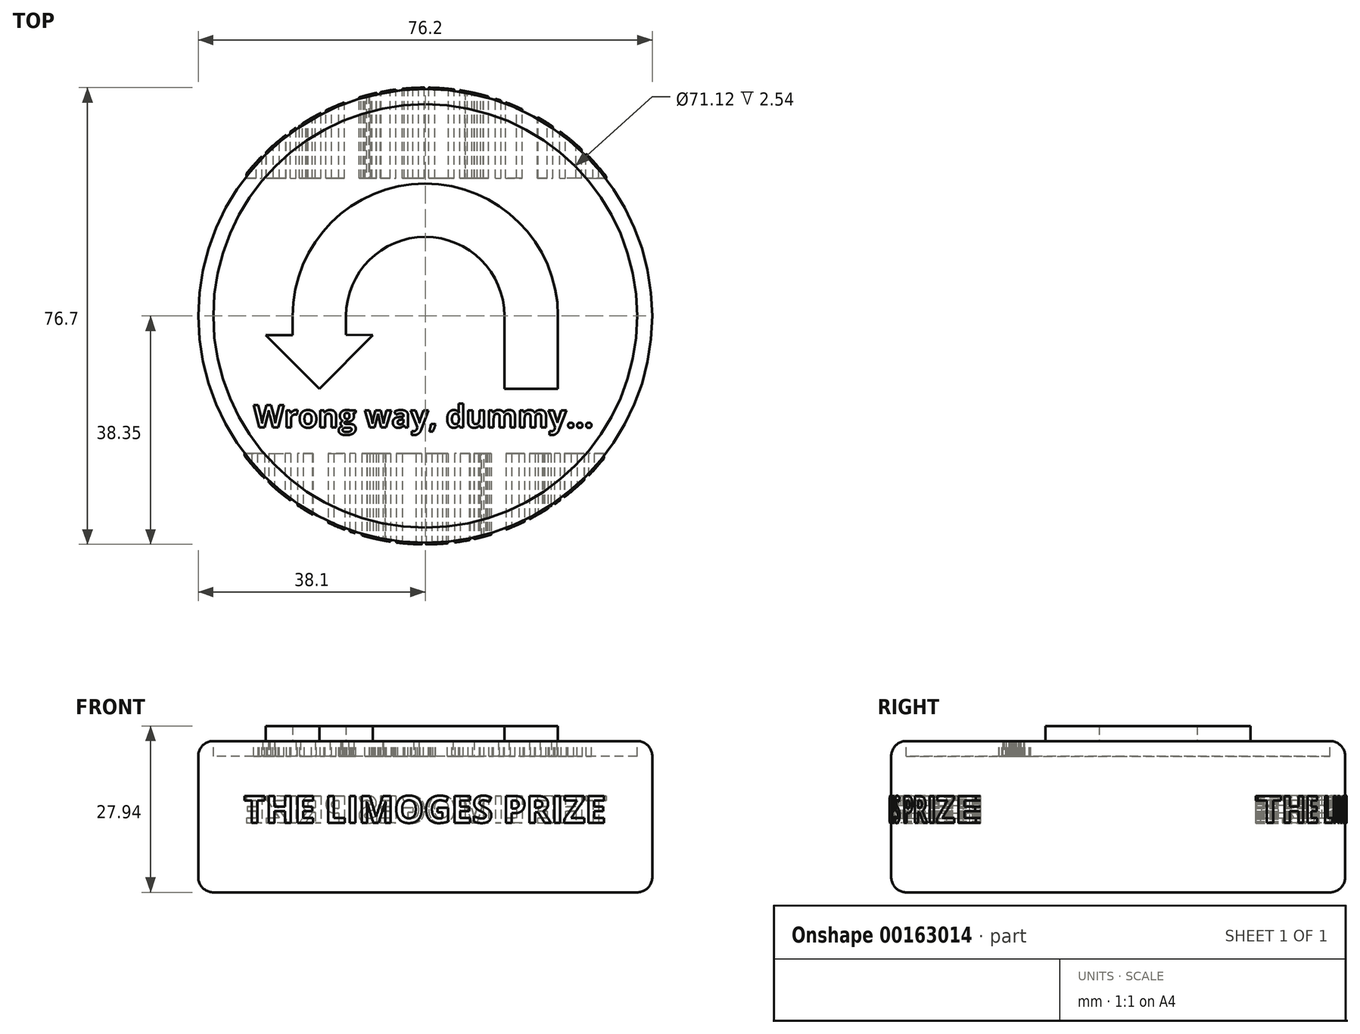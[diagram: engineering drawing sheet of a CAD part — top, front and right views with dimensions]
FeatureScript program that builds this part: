
annotation { "Feature Type Name" : "Feature", "Feature Type Description" : "" }
export const myFeature = defineFeature(function(context is Context, id is Id, definition is map)
    precondition{}
    {
        {
            var Q0;
            Q0=qCreatedBy(makeId("Top.planeOp"),FACE);
            var sketch = newSketch(context, id + "F0", { "sketchPlane" : qUnion([Q0])});
            skCircle(sketch, "E0", {"center": v(0, 0) * mm, "radius": 38.1 * mm});
            skSolve(sketch);
        }
        {
            var Q0;
            Q0 = qSketchRegion(id + "F0", true);
            var Q1;
            Q1=makeQuery(id+"F0.imprint","IMPRINT",FACE,{"disambiguationData":[TD([[makeQuery(id+"F0.imprint","IMPRINT",EDGE,{"derivedFrom":sQuery(id+"F0.wireOp",EDGE,"E0")}),1.0]])]});
            extrude(context, id + "F1", {"entities" : qUnion([Q0, Q1]), "depth" : 25.4 * mm});
        }
        {
            var Q0;
            Q0=makeQuery(id+"F1.opExtrude","CAP_EDGE",EDGE,{"disambiguationData":[OSD([sQuery(id+"F0.wireOp",EDGE,"E0")])],"isStart":false});
            var Q1;
            Q1=makeQuery(id+"F1.opExtrude","CAP_EDGE",EDGE,{"disambiguationData":[OSD([sQuery(id+"F0.wireOp",EDGE,"E0")])],"isStart":true});
            fillet(context, id + "F2", {"entities" : qUnion([Q0, Q1]), "radius" : 2.54 * mm, "tangentPropagation" : true, "allowEdgeOverflow" : false});
        }
        {
            var Q0;
            Q0=makeQuery(id+"F1.opExtrude","CAP_FACE",FACE,{"disambiguationData":[OSD([sQuery(id+"F0.wireOp",EDGE,"E0")])],"isStart":false});
            var sketch = newSketch(context, id + "F3", { "sketchPlane" : qUnion([Q0])});
            skLineSegment(sketch, "E1", {"start": v(-17.78, -12.2) * mm, "end": v(-22.28, -7.7) * mm});
            skLineSegment(sketch, "E2", {"start": v(-17.78, -12.2) * mm, "end": v(-13.28, -7.7) * mm});
            skLineSegment(sketch, "E3", {"start": v(-13.28, -7.7) * mm, "end": v(-8.8, -3.22) * mm});
            skLineSegment(sketch, "E4", {"start": v(-22.28, -7.7) * mm, "end": v(-26.76, -3.22) * mm});
            skLineSegment(sketch, "E5", {"start": v(-26.76, -3.22) * mm, "end": v(-22.28, -3.22) * mm});
            skLineSegment(sketch, "E6", {"start": v(-8.8, -3.22) * mm, "end": v(-13.28, -3.18) * mm});
            skLineSegment(sketch, "E7", {"start": v(17.78, -12.2) * mm, "end": v(22.28, -12.2) * mm});
            skLineSegment(sketch, "E8", {"start": v(17.78, -12.2) * mm, "end": v(13.28, -12.2) * mm});
            skLineSegment(sketch, "E9", {"start": v(13.28, -12.2) * mm, "end": v(13.28, 0) * mm});
            skLineSegment(sketch, "E10", {"start": v(22.28, -12.2) * mm, "end": v(22.28, 0) * mm});
            skLineSegment(sketch, "E11", {"start": v(-13.28, -3.18) * mm, "end": v(-13.28, 0) * mm});
            skLineSegment(sketch, "E12", {"start": v(-22.28, -3.22) * mm, "end": v(-22.28, -0.05) * mm});
            skArc(sketch, "E13", {"start": v(-22.28, -0.05) * mm, "mid": v(-0.02, 22.23) * mm, "end": v(22.28, 0) * mm});
            skArc(sketch, "E14", {"start": v(-13.28, 0) * mm, "mid": v(0, 13.28) * mm, "end": v(13.28, 0) * mm});
            skText(sketch, "E15", { "text": "Wrong way, dummy...", "fontName": "OpenSans-Bold.ttf"});
            const initialGuessF3  = {"E15": [-0.02883, -0.01873, 1, 0, 0.00381]};
            skSetInitialGuess(sketch, initialGuessF3);
            skSolve(sketch);
        }
        {
            var Q0;
            Q0=makeQuery(id+"F3.imprint","IMPRINT",FACE,{"disambiguationData":[TD([[makeQuery(id+"F3.imprint","IMPRINT",EDGE,{"derivedFrom":sQuery(id+"F3.wireOp",EDGE,"E1")}),-1.0]])]});
            var Q1;
            Q1=makeQuery(id+"F3.imprint","IMPRINT",FACE,{"disambiguationData":[TD([[makeQuery(id+"F3.imprint","IMPRINT",EDGE,{"derivedFrom":sQuery(id+"F3.wireOp",EDGE,"E1")}),1.0]])]});
            extrude(context, id + "F4", {"entities" : qUnion([Q0, Q1]), "operationType" : NewBodyOperationType.REMOVE, "oppositeDirection" : true, "depth" : 2.54 * mm});
        }
        {
            var Q0;
            Q0=makeQuery(id+"F3.imprint","IMPRINT",FACE,{"disambiguationData":[TD([[makeQuery(id+"F3.imprint","IMPRINT",EDGE,{"derivedFrom":sQuery(id+"F3.wireOp",EDGE,"E1")}),-1.0]])]});
            extrude(context, id + "F5", {"entities" : qUnion([Q0]), "operationType" : NewBodyOperationType.ADD, "depth" : 2.54 * mm});
        }
        {
            var Q0;
            Q0=makeQuery(id+"F3.imprint","IMPRINT",FACE,{"disambiguationData":[TD([[makeQuery(id+"F3.imprint","IMPRINT",EDGE,{"derivedFrom":sQuery(id+"F3.wireOp",EDGE,"E15.sketch_text.stroke-160")}),1.0]])]});
            var Q1;
            Q1=makeQuery(id+"F3.imprint","IMPRINT",FACE,{"disambiguationData":[TD([[makeQuery(id+"F3.imprint","IMPRINT",EDGE,{"derivedFrom":sQuery(id+"F3.wireOp",EDGE,"E15.sketch_text.stroke-110")}),1.0]])]});
            var Q2;
            Q2=makeQuery(id+"F3.imprint","IMPRINT",FACE,{"disambiguationData":[TD([[makeQuery(id+"F3.imprint","IMPRINT",EDGE,{"derivedFrom":sQuery(id+"F3.wireOp",EDGE,"E15.sketch_text.stroke-101")}),1.0]])]});
            var Q3;
            Q3=makeQuery(id+"F3.imprint","IMPRINT",FACE,{"disambiguationData":[TD([[makeQuery(id+"F3.imprint","IMPRINT",EDGE,{"derivedFrom":sQuery(id+"F3.wireOp",EDGE,"E15.sketch_text.stroke-37")}),1.0]])]});
            var Q4;
            Q4=makeQuery(id+"F3.imprint","IMPRINT",FACE,{"disambiguationData":[TD([[makeQuery(id+"F3.imprint","IMPRINT",EDGE,{"derivedFrom":sQuery(id+"F3.wireOp",EDGE,"E15.sketch_text.stroke-203")}),1.0]])]});
            extrude(context, id + "F6", {"entities" : qUnion([Q0, Q1, Q2, Q3, Q4]), "operationType" : NewBodyOperationType.REMOVE, "oppositeDirection" : true, "depth" : 2.54 * mm});
        }
        {
            var Q0;
            Q0=qCreatedBy(makeId("Front.planeOp"),FACE);
            cPlane(context, id + "F7", {"entities" : qUnion([Q0]), "cplaneType" : CPlaneType.OFFSET, "offset" : 38.35 * mm, "width" : 152.4 * mm, "height" : 152.4 * mm});
        }
        {
            var Q0;
            Q0=qCreatedBy(id+"F7.planeOp",FACE);
            var sketch = newSketch(context, id + "F8", { "sketchPlane" : qUnion([Q0])});
            skText(sketch, "E16", { "text": "THE LIMOGES PRIZE", "fontName": "OpenSans-Bold.ttf"});
            const initialGuessF8  = {"E16": [-0.03048, 0.01168, 1, 0, 0.00454]};
            skSetInitialGuess(sketch, initialGuessF8);
            skSolve(sketch);
        }
        {
            var Q0;
            Q0 = qSketchRegion(id + "F8", true);
            extrude(context, id + "F9", {"entities" : qUnion([Q0]), "oppositeDirection" : true, "depth" : 15.24 * mm});
        }
        {
            var Q0;
            Q0=qCreatedBy(makeId("Top.planeOp"),FACE);
            var sketch = newSketch(context, id + "F10", { "sketchPlane" : qUnion([Q0])});
            skCircle(sketch, "E17", {"center": v(0, 0) * mm, "radius": 38.35 * mm});
            skCircle(sketch, "E18", {"center": v(0, 0) * mm, "radius": 50.53 * mm});
            skSolve(sketch);
        }
        {
            var Q0;
            Q0 = qSketchRegion(id + "F10", true);
            var Q1;
            Q1=makeQuery(id+"F10.imprint","IMPRINT",FACE,{"disambiguationData":[TD([[makeQuery(id+"F10.imprint","IMPRINT",EDGE,{"derivedFrom":sQuery(id+"F10.wireOp",EDGE,"E17")}),-1.0]])]});
            extrude(context, id + "F11", {"entities" : qUnion([Q0, Q1]), "operationType" : NewBodyOperationType.REMOVE, "depth" : 25.4 * mm});
        }
        {
            var Q0;
            Q0=qCreatedBy(makeId("Front.planeOp"),FACE);
            var sketch = newSketch(context, id + "F12", { "sketchPlane" : qUnion([Q0])});
            skLineSegment(sketch, "E19", {"start": v(0, 0) * mm, "end": v(0, -28.54) * mm});
            skSolve(sketch);
        }
        {
            var Q0;
            Q0=makeQuery(id+"F9.opExtrude","SWEPT_BODY",BODY,{"disambiguationData":[OSD([sQuery(id+"F8.wireOp",EDGE,"E16.sketch_text.stroke-0"),sQuery(id+"F8.wireOp",EDGE,"E16.sketch_text.stroke-1"),sQuery(id+"F8.wireOp",EDGE,"E16.sketch_text.stroke-2"),sQuery(id+"F8.wireOp",EDGE,"E16.sketch_text.stroke-3"),sQuery(id+"F8.wireOp",EDGE,"E16.sketch_text.stroke-4"),sQuery(id+"F8.wireOp",EDGE,"E16.sketch_text.stroke-5"),sQuery(id+"F8.wireOp",EDGE,"E16.sketch_text.stroke-6"),sQuery(id+"F8.wireOp",EDGE,"E16.sketch_text.stroke-7")])]});
            var Q1;
            Q1=makeQuery(id+"F9.opExtrude","SWEPT_BODY",BODY,{"disambiguationData":[OSD([sQuery(id+"F8.wireOp",EDGE,"E16.sketch_text.stroke-8"),sQuery(id+"F8.wireOp",EDGE,"E16.sketch_text.stroke-9"),sQuery(id+"F8.wireOp",EDGE,"E16.sketch_text.stroke-10"),sQuery(id+"F8.wireOp",EDGE,"E16.sketch_text.stroke-11"),sQuery(id+"F8.wireOp",EDGE,"E16.sketch_text.stroke-12"),sQuery(id+"F8.wireOp",EDGE,"E16.sketch_text.stroke-13"),sQuery(id+"F8.wireOp",EDGE,"E16.sketch_text.stroke-14"),sQuery(id+"F8.wireOp",EDGE,"E16.sketch_text.stroke-15"),sQuery(id+"F8.wireOp",EDGE,"E16.sketch_text.stroke-16"),sQuery(id+"F8.wireOp",EDGE,"E16.sketch_text.stroke-17"),sQuery(id+"F8.wireOp",EDGE,"E16.sketch_text.stroke-18"),sQuery(id+"F8.wireOp",EDGE,"E16.sketch_text.stroke-19")])]});
            var Q2;
            Q2=makeQuery(id+"F9.opExtrude","SWEPT_BODY",BODY,{"disambiguationData":[OSD([sQuery(id+"F8.wireOp",EDGE,"E16.sketch_text.stroke-20"),sQuery(id+"F8.wireOp",EDGE,"E16.sketch_text.stroke-21"),sQuery(id+"F8.wireOp",EDGE,"E16.sketch_text.stroke-22"),sQuery(id+"F8.wireOp",EDGE,"E16.sketch_text.stroke-23"),sQuery(id+"F8.wireOp",EDGE,"E16.sketch_text.stroke-24"),sQuery(id+"F8.wireOp",EDGE,"E16.sketch_text.stroke-25"),sQuery(id+"F8.wireOp",EDGE,"E16.sketch_text.stroke-26"),sQuery(id+"F8.wireOp",EDGE,"E16.sketch_text.stroke-27"),sQuery(id+"F8.wireOp",EDGE,"E16.sketch_text.stroke-28"),sQuery(id+"F8.wireOp",EDGE,"E16.sketch_text.stroke-29"),sQuery(id+"F8.wireOp",EDGE,"E16.sketch_text.stroke-30"),sQuery(id+"F8.wireOp",EDGE,"E16.sketch_text.stroke-31")])]});
            var Q3;
            Q3=makeQuery(id+"F9.opExtrude","SWEPT_BODY",BODY,{"disambiguationData":[OSD([sQuery(id+"F8.wireOp",EDGE,"E16.sketch_text.stroke-32"),sQuery(id+"F8.wireOp",EDGE,"E16.sketch_text.stroke-33"),sQuery(id+"F8.wireOp",EDGE,"E16.sketch_text.stroke-34"),sQuery(id+"F8.wireOp",EDGE,"E16.sketch_text.stroke-35"),sQuery(id+"F8.wireOp",EDGE,"E16.sketch_text.stroke-36"),sQuery(id+"F8.wireOp",EDGE,"E16.sketch_text.stroke-37")])]});
            var Q4;
            Q4=makeQuery(id+"F9.opExtrude","SWEPT_BODY",BODY,{"disambiguationData":[OSD([sQuery(id+"F8.wireOp",EDGE,"E16.sketch_text.stroke-38"),sQuery(id+"F8.wireOp",EDGE,"E16.sketch_text.stroke-39"),sQuery(id+"F8.wireOp",EDGE,"E16.sketch_text.stroke-40"),sQuery(id+"F8.wireOp",EDGE,"E16.sketch_text.stroke-41")])]});
            var Q5;
            Q5=makeQuery(id+"F9.opExtrude","SWEPT_BODY",BODY,{"disambiguationData":[OSD([sQuery(id+"F8.wireOp",EDGE,"E16.sketch_text.stroke-42"),sQuery(id+"F8.wireOp",EDGE,"E16.sketch_text.stroke-43"),sQuery(id+"F8.wireOp",EDGE,"E16.sketch_text.stroke-44"),sQuery(id+"F8.wireOp",EDGE,"E16.sketch_text.stroke-45"),sQuery(id+"F8.wireOp",EDGE,"E16.sketch_text.stroke-46"),sQuery(id+"F8.wireOp",EDGE,"E16.sketch_text.stroke-47"),sQuery(id+"F8.wireOp",EDGE,"E16.sketch_text.stroke-48"),sQuery(id+"F8.wireOp",EDGE,"E16.sketch_text.stroke-49"),sQuery(id+"F8.wireOp",EDGE,"E16.sketch_text.stroke-50"),sQuery(id+"F8.wireOp",EDGE,"E16.sketch_text.stroke-51"),sQuery(id+"F8.wireOp",EDGE,"E16.sketch_text.stroke-52"),sQuery(id+"F8.wireOp",EDGE,"E16.sketch_text.stroke-53"),sQuery(id+"F8.wireOp",EDGE,"E16.sketch_text.stroke-54"),sQuery(id+"F8.wireOp",EDGE,"E16.sketch_text.stroke-55"),sQuery(id+"F8.wireOp",EDGE,"E16.sketch_text.stroke-56"),sQuery(id+"F8.wireOp",EDGE,"E16.sketch_text.stroke-57"),sQuery(id+"F8.wireOp",EDGE,"E16.sketch_text.stroke-58"),sQuery(id+"F8.wireOp",EDGE,"E16.sketch_text.stroke-59"),sQuery(id+"F8.wireOp",EDGE,"E16.sketch_text.stroke-60")])]});
            var Q6;
            Q6=makeQuery(id+"F9.opExtrude","SWEPT_BODY",BODY,{"disambiguationData":[OSD([sQuery(id+"F8.wireOp",EDGE,"E16.sketch_text.stroke-61"),sQuery(id+"F8.wireOp",EDGE,"E16.sketch_text.stroke-62"),sQuery(id+"F8.wireOp",EDGE,"E16.sketch_text.stroke-63"),sQuery(id+"F8.wireOp",EDGE,"E16.sketch_text.stroke-64"),sQuery(id+"F8.wireOp",EDGE,"E16.sketch_text.stroke-65"),sQuery(id+"F8.wireOp",EDGE,"E16.sketch_text.stroke-66"),sQuery(id+"F8.wireOp",EDGE,"E16.sketch_text.stroke-67"),sQuery(id+"F8.wireOp",EDGE,"E16.sketch_text.stroke-68"),sQuery(id+"F8.wireOp",EDGE,"E16.sketch_text.stroke-69"),sQuery(id+"F8.wireOp",EDGE,"E16.sketch_text.stroke-70"),sQuery(id+"F8.wireOp",EDGE,"E16.sketch_text.stroke-71"),sQuery(id+"F8.wireOp",EDGE,"E16.sketch_text.stroke-72"),sQuery(id+"F8.wireOp",EDGE,"E16.sketch_text.stroke-73"),sQuery(id+"F8.wireOp",EDGE,"E16.sketch_text.stroke-74")])]});
            var Q7;
            Q7=makeQuery(id+"F9.opExtrude","SWEPT_BODY",BODY,{"disambiguationData":[OSD([sQuery(id+"F8.wireOp",EDGE,"E16.sketch_text.stroke-75"),sQuery(id+"F8.wireOp",EDGE,"E16.sketch_text.stroke-76"),sQuery(id+"F8.wireOp",EDGE,"E16.sketch_text.stroke-77"),sQuery(id+"F8.wireOp",EDGE,"E16.sketch_text.stroke-78"),sQuery(id+"F8.wireOp",EDGE,"E16.sketch_text.stroke-79"),sQuery(id+"F8.wireOp",EDGE,"E16.sketch_text.stroke-80"),sQuery(id+"F8.wireOp",EDGE,"E16.sketch_text.stroke-81"),sQuery(id+"F8.wireOp",EDGE,"E16.sketch_text.stroke-82"),sQuery(id+"F8.wireOp",EDGE,"E16.sketch_text.stroke-83"),sQuery(id+"F8.wireOp",EDGE,"E16.sketch_text.stroke-84"),sQuery(id+"F8.wireOp",EDGE,"E16.sketch_text.stroke-85"),sQuery(id+"F8.wireOp",EDGE,"E16.sketch_text.stroke-86"),sQuery(id+"F8.wireOp",EDGE,"E16.sketch_text.stroke-87"),sQuery(id+"F8.wireOp",EDGE,"E16.sketch_text.stroke-88"),sQuery(id+"F8.wireOp",EDGE,"E16.sketch_text.stroke-89"),sQuery(id+"F8.wireOp",EDGE,"E16.sketch_text.stroke-90"),sQuery(id+"F8.wireOp",EDGE,"E16.sketch_text.stroke-91"),sQuery(id+"F8.wireOp",EDGE,"E16.sketch_text.stroke-92"),sQuery(id+"F8.wireOp",EDGE,"E16.sketch_text.stroke-93")])]});
            var Q8;
            Q8=makeQuery(id+"F9.opExtrude","SWEPT_BODY",BODY,{"disambiguationData":[OSD([sQuery(id+"F8.wireOp",EDGE,"E16.sketch_text.stroke-94"),sQuery(id+"F8.wireOp",EDGE,"E16.sketch_text.stroke-95"),sQuery(id+"F8.wireOp",EDGE,"E16.sketch_text.stroke-96"),sQuery(id+"F8.wireOp",EDGE,"E16.sketch_text.stroke-97"),sQuery(id+"F8.wireOp",EDGE,"E16.sketch_text.stroke-98"),sQuery(id+"F8.wireOp",EDGE,"E16.sketch_text.stroke-99"),sQuery(id+"F8.wireOp",EDGE,"E16.sketch_text.stroke-100"),sQuery(id+"F8.wireOp",EDGE,"E16.sketch_text.stroke-101"),sQuery(id+"F8.wireOp",EDGE,"E16.sketch_text.stroke-102"),sQuery(id+"F8.wireOp",EDGE,"E16.sketch_text.stroke-103"),sQuery(id+"F8.wireOp",EDGE,"E16.sketch_text.stroke-104"),sQuery(id+"F8.wireOp",EDGE,"E16.sketch_text.stroke-105")])]});
            var Q9;
            Q9=makeQuery(id+"F9.opExtrude","SWEPT_BODY",BODY,{"disambiguationData":[OSD([sQuery(id+"F8.wireOp",EDGE,"E16.sketch_text.stroke-106"),sQuery(id+"F8.wireOp",EDGE,"E16.sketch_text.stroke-107"),sQuery(id+"F8.wireOp",EDGE,"E16.sketch_text.stroke-108"),sQuery(id+"F8.wireOp",EDGE,"E16.sketch_text.stroke-109"),sQuery(id+"F8.wireOp",EDGE,"E16.sketch_text.stroke-110"),sQuery(id+"F8.wireOp",EDGE,"E16.sketch_text.stroke-111"),sQuery(id+"F8.wireOp",EDGE,"E16.sketch_text.stroke-112"),sQuery(id+"F8.wireOp",EDGE,"E16.sketch_text.stroke-113"),sQuery(id+"F8.wireOp",EDGE,"E16.sketch_text.stroke-114"),sQuery(id+"F8.wireOp",EDGE,"E16.sketch_text.stroke-115"),sQuery(id+"F8.wireOp",EDGE,"E16.sketch_text.stroke-116"),sQuery(id+"F8.wireOp",EDGE,"E16.sketch_text.stroke-117"),sQuery(id+"F8.wireOp",EDGE,"E16.sketch_text.stroke-118"),sQuery(id+"F8.wireOp",EDGE,"E16.sketch_text.stroke-119"),sQuery(id+"F8.wireOp",EDGE,"E16.sketch_text.stroke-120"),sQuery(id+"F8.wireOp",EDGE,"E16.sketch_text.stroke-121"),sQuery(id+"F8.wireOp",EDGE,"E16.sketch_text.stroke-122"),sQuery(id+"F8.wireOp",EDGE,"E16.sketch_text.stroke-123"),sQuery(id+"F8.wireOp",EDGE,"E16.sketch_text.stroke-124"),sQuery(id+"F8.wireOp",EDGE,"E16.sketch_text.stroke-125"),sQuery(id+"F8.wireOp",EDGE,"E16.sketch_text.stroke-126"),sQuery(id+"F8.wireOp",EDGE,"E16.sketch_text.stroke-127"),sQuery(id+"F8.wireOp",EDGE,"E16.sketch_text.stroke-128"),sQuery(id+"F8.wireOp",EDGE,"E16.sketch_text.stroke-129"),sQuery(id+"F8.wireOp",EDGE,"E16.sketch_text.stroke-130"),sQuery(id+"F8.wireOp",EDGE,"E16.sketch_text.stroke-131"),sQuery(id+"F8.wireOp",EDGE,"E16.sketch_text.stroke-132"),sQuery(id+"F8.wireOp",EDGE,"E16.sketch_text.stroke-133")])]});
            var Q10;
            Q10=makeQuery(id+"F9.opExtrude","SWEPT_BODY",BODY,{"disambiguationData":[OSD([sQuery(id+"F8.wireOp",EDGE,"E16.sketch_text.stroke-134"),sQuery(id+"F8.wireOp",EDGE,"E16.sketch_text.stroke-135"),sQuery(id+"F8.wireOp",EDGE,"E16.sketch_text.stroke-136"),sQuery(id+"F8.wireOp",EDGE,"E16.sketch_text.stroke-137"),sQuery(id+"F8.wireOp",EDGE,"E16.sketch_text.stroke-138"),sQuery(id+"F8.wireOp",EDGE,"E16.sketch_text.stroke-139"),sQuery(id+"F8.wireOp",EDGE,"E16.sketch_text.stroke-140"),sQuery(id+"F8.wireOp",EDGE,"E16.sketch_text.stroke-141"),sQuery(id+"F8.wireOp",EDGE,"E16.sketch_text.stroke-142"),sQuery(id+"F8.wireOp",EDGE,"E16.sketch_text.stroke-143"),sQuery(id+"F8.wireOp",EDGE,"E16.sketch_text.stroke-144"),sQuery(id+"F8.wireOp",EDGE,"E16.sketch_text.stroke-145"),sQuery(id+"F8.wireOp",EDGE,"E16.sketch_text.stroke-146"),sQuery(id+"F8.wireOp",EDGE,"E16.sketch_text.stroke-147"),sQuery(id+"F8.wireOp",EDGE,"E16.sketch_text.stroke-148"),sQuery(id+"F8.wireOp",EDGE,"E16.sketch_text.stroke-149")])]});
            var Q11;
            Q11=makeQuery(id+"F9.opExtrude","SWEPT_BODY",BODY,{"disambiguationData":[OSD([sQuery(id+"F8.wireOp",EDGE,"E16.sketch_text.stroke-150"),sQuery(id+"F8.wireOp",EDGE,"E16.sketch_text.stroke-151"),sQuery(id+"F8.wireOp",EDGE,"E16.sketch_text.stroke-152"),sQuery(id+"F8.wireOp",EDGE,"E16.sketch_text.stroke-153"),sQuery(id+"F8.wireOp",EDGE,"E16.sketch_text.stroke-154"),sQuery(id+"F8.wireOp",EDGE,"E16.sketch_text.stroke-155"),sQuery(id+"F8.wireOp",EDGE,"E16.sketch_text.stroke-156"),sQuery(id+"F8.wireOp",EDGE,"E16.sketch_text.stroke-157"),sQuery(id+"F8.wireOp",EDGE,"E16.sketch_text.stroke-158"),sQuery(id+"F8.wireOp",EDGE,"E16.sketch_text.stroke-159"),sQuery(id+"F8.wireOp",EDGE,"E16.sketch_text.stroke-160"),sQuery(id+"F8.wireOp",EDGE,"E16.sketch_text.stroke-161"),sQuery(id+"F8.wireOp",EDGE,"E16.sketch_text.stroke-162"),sQuery(id+"F8.wireOp",EDGE,"E16.sketch_text.stroke-163"),sQuery(id+"F8.wireOp",EDGE,"E16.sketch_text.stroke-164"),sQuery(id+"F8.wireOp",EDGE,"E16.sketch_text.stroke-165"),sQuery(id+"F8.wireOp",EDGE,"E16.sketch_text.stroke-166"),sQuery(id+"F8.wireOp",EDGE,"E16.sketch_text.stroke-167"),sQuery(id+"F8.wireOp",EDGE,"E16.sketch_text.stroke-168")])]});
            var Q12;
            Q12=makeQuery(id+"F9.opExtrude","SWEPT_BODY",BODY,{"disambiguationData":[OSD([sQuery(id+"F8.wireOp",EDGE,"E16.sketch_text.stroke-169"),sQuery(id+"F8.wireOp",EDGE,"E16.sketch_text.stroke-170"),sQuery(id+"F8.wireOp",EDGE,"E16.sketch_text.stroke-171"),sQuery(id+"F8.wireOp",EDGE,"E16.sketch_text.stroke-172")])]});
            var Q13;
            Q13=makeQuery(id+"F9.opExtrude","SWEPT_BODY",BODY,{"disambiguationData":[OSD([sQuery(id+"F8.wireOp",EDGE,"E16.sketch_text.stroke-173"),sQuery(id+"F8.wireOp",EDGE,"E16.sketch_text.stroke-174"),sQuery(id+"F8.wireOp",EDGE,"E16.sketch_text.stroke-175"),sQuery(id+"F8.wireOp",EDGE,"E16.sketch_text.stroke-176"),sQuery(id+"F8.wireOp",EDGE,"E16.sketch_text.stroke-177"),sQuery(id+"F8.wireOp",EDGE,"E16.sketch_text.stroke-178"),sQuery(id+"F8.wireOp",EDGE,"E16.sketch_text.stroke-179"),sQuery(id+"F8.wireOp",EDGE,"E16.sketch_text.stroke-180"),sQuery(id+"F8.wireOp",EDGE,"E16.sketch_text.stroke-181"),sQuery(id+"F8.wireOp",EDGE,"E16.sketch_text.stroke-182")])]});
            var Q14;
            Q14=makeQuery(id+"F9.opExtrude","SWEPT_BODY",BODY,{"disambiguationData":[OSD([sQuery(id+"F8.wireOp",EDGE,"E16.sketch_text.stroke-183"),sQuery(id+"F8.wireOp",EDGE,"E16.sketch_text.stroke-184"),sQuery(id+"F8.wireOp",EDGE,"E16.sketch_text.stroke-185"),sQuery(id+"F8.wireOp",EDGE,"E16.sketch_text.stroke-186"),sQuery(id+"F8.wireOp",EDGE,"E16.sketch_text.stroke-187"),sQuery(id+"F8.wireOp",EDGE,"E16.sketch_text.stroke-188"),sQuery(id+"F8.wireOp",EDGE,"E16.sketch_text.stroke-189"),sQuery(id+"F8.wireOp",EDGE,"E16.sketch_text.stroke-190"),sQuery(id+"F8.wireOp",EDGE,"E16.sketch_text.stroke-191"),sQuery(id+"F8.wireOp",EDGE,"E16.sketch_text.stroke-192"),sQuery(id+"F8.wireOp",EDGE,"E16.sketch_text.stroke-193"),sQuery(id+"F8.wireOp",EDGE,"E16.sketch_text.stroke-194")])]});
            var Q15;
            Q15=sQuery(id+"F12.wireOp",EDGE,"E19");
            circularPattern(context, id + "F13", {"entities" : qUnion([Q0, Q1, Q2, Q3, Q4, Q5, Q6, Q7, Q8, Q9, Q10, Q11, Q12, Q13, Q14]), "axis" : qUnion([Q15]), "angle" : 180 * degree, "instanceCount" : 2});
        }
    });
